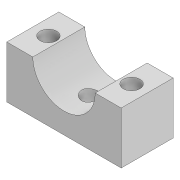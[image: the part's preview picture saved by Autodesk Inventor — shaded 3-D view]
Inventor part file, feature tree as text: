
AUTODESK INVENTOR PART (.ipt)
format: ipt  version: 2022 (Build 260153000, 153)  size: 119,808 bytes
history: native  units: mm
features: extrude x3, sketch x3
ambient origin geometry x8: Origin, YZ Plane, XZ Plane, XY Plane, X Axis, Y Axis, Z Axis, Center Point
bodies: Solid1 (feature_tree)
feature tree (6):
  extrude  "Extrusion1"  Depth=11.0mm
  extrude  "Extrusion2"  Depth=10.0mm
  extrude  "Extrusion3"  Depth=10.0mm TaperAngle=0.0deg
  sketch  "Sketch2"  dims[d0=12.0mm d1=11.0mm]
  sketch  "Sketch3"  dims[d2=11.0mm d3=10.0mm]
  sketch  "Sketch4"  dims[d4=3.0mm d5=10.0mm d6=0.0mm d7=3.2mm d8=3.0mm d9=5.0mm d10=3.2mm d11=3.0mm d12=5.0mm d13=10.0mm d14=0.0mm d15=3.2mm d16=5.0mm d17=10.0mm d18=0.0mm]
